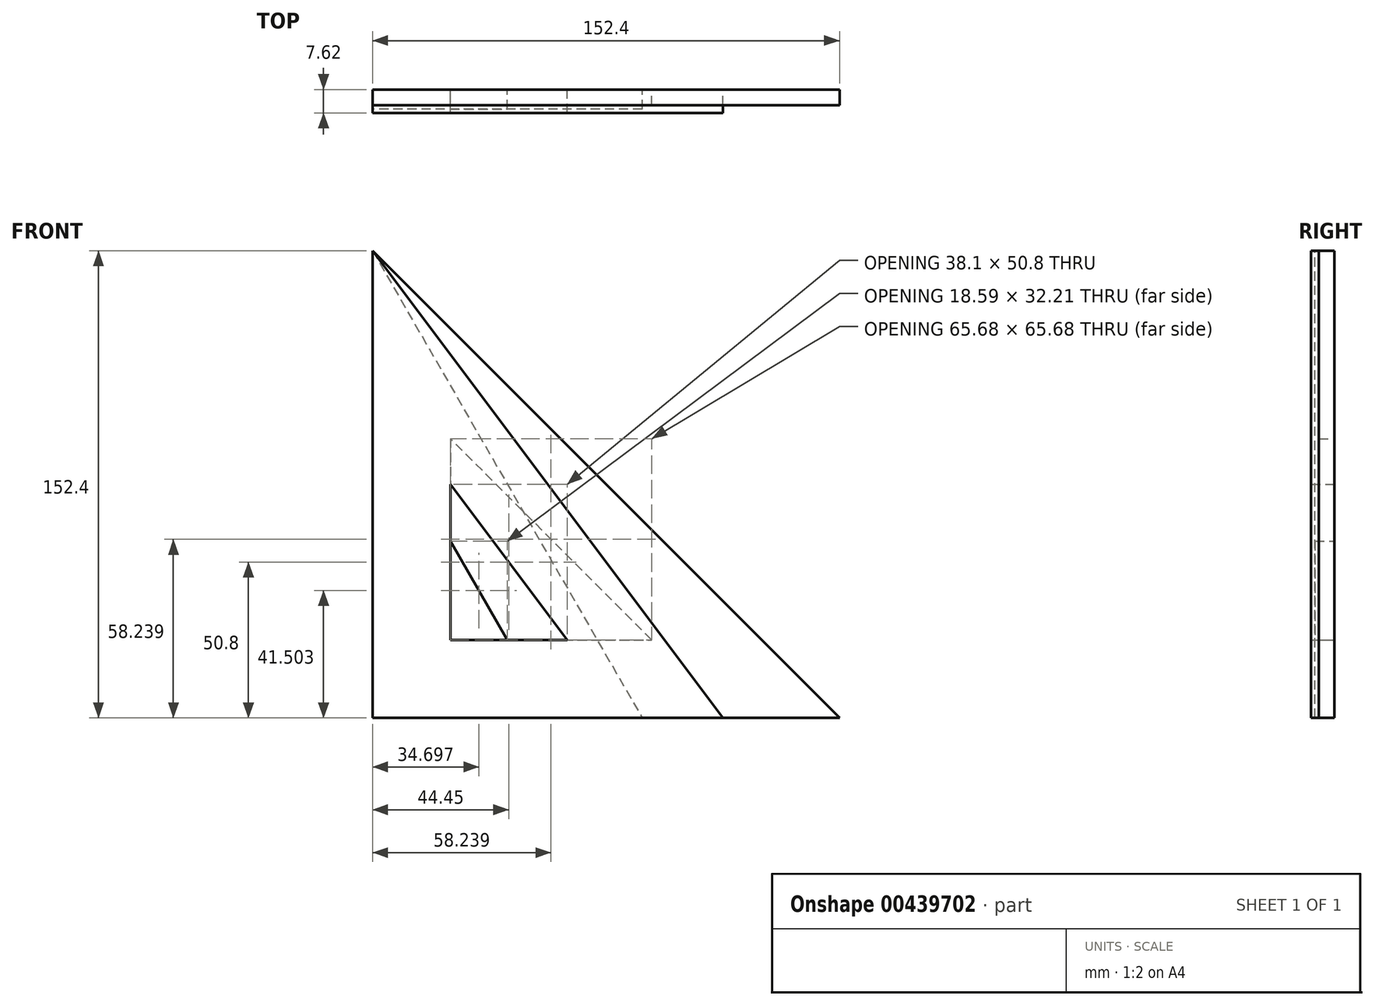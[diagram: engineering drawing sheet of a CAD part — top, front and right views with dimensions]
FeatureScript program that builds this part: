
annotation { "Feature Type Name" : "Feature", "Feature Type Description" : "" }
export const myFeature = defineFeature(function(context is Context, id is Id, definition is map)
    precondition{}
    {
        {
            var Q0;
            Q0=qCreatedBy(makeId("Front.planeOp"),FACE);
            var sketch = newSketch(context, id + "F0", { "sketchPlane" : qUnion([Q0])});
            skLineSegment(sketch, "E0", {"start": v(0, 0) * mm, "end": v(152.4, 0) * mm});
            skLineSegment(sketch, "E1", {"start": v(0, 152.4) * mm, "end": v(0, 0) * mm});
            skLineSegment(sketch, "E2", {"start": v(25.4, 25.4) * mm, "end": v(91.08, 25.4) * mm});
            skLineSegment(sketch, "E3", {"start": v(91.08, 25.4) * mm, "end": v(25.4, 91.08) * mm});
            skLineSegment(sketch, "E4", {"start": v(25.4, 91.08) * mm, "end": v(25.4, 25.4) * mm});
            skLineSegment(sketch, "E5", {"start": v(0, 152.4) * mm, "end": v(152.4, 0) * mm});
            skSolve(sketch);
        }
        {
            var Q0;
            Q0=makeQuery(id+"F0.imprint","IMPRINT",FACE,{"disambiguationData":[TD([[makeQuery(id+"F0.imprint","IMPRINT",EDGE,{"derivedFrom":sQuery(id+"F0.wireOp",EDGE,"E0")}),1.0]])]});
            extrude(context, id + "F1", {"entities" : qUnion([Q0]), "depth" : 5.08 * mm});
        }
        {
            var Q0;
            Q0=qCreatedBy(makeId("Front.planeOp"),FACE);
            var sketch = newSketch(context, id + "F2", { "sketchPlane" : qUnion([Q0])});
            skLineSegment(sketch, "E6", {"start": v(0, 0) * mm, "end": v(0, 152.4) * mm});
            skLineSegment(sketch, "E7", {"start": v(0, 152.4) * mm, "end": v(87.99, 0) * mm});
            skLineSegment(sketch, "E8", {"start": v(87.99, 0) * mm, "end": v(0, 0) * mm});
            skLineSegment(sketch, "E9", {"start": v(25.4, 25.4) * mm, "end": v(44, 25.4) * mm});
            skLineSegment(sketch, "E10", {"start": v(44, 25.4) * mm, "end": v(25.4, 57.6) * mm});
            skLineSegment(sketch, "E11", {"start": v(25.4, 57.6) * mm, "end": v(25.4, 25.4) * mm});
            skSolve(sketch);
        }
        {
            var Q0;
            Q0 = qSketchRegion(id + "F2", true);
            extrude(context, id + "F3", {"entities" : qUnion([Q0]), "depth" : 6.35 * mm});
        }
        {
            var Q0;
            Q0=qCreatedBy(makeId("Front.planeOp"),FACE);
            var sketch = newSketch(context, id + "F4", { "sketchPlane" : qUnion([Q0])});
            skLineSegment(sketch, "E12", {"start": v(0, 0) * mm, "end": v(0, 152.4) * mm});
            skLineSegment(sketch, "E13", {"start": v(0, 152.4) * mm, "end": v(114.3, 0) * mm});
            skLineSegment(sketch, "E14", {"start": v(114.3, 0) * mm, "end": v(0, 0) * mm});
            skLineSegment(sketch, "E15", {"start": v(25.4, 25.4) * mm, "end": v(63.5, 25.4) * mm});
            skLineSegment(sketch, "E16", {"start": v(63.5, 25.4) * mm, "end": v(25.4, 76.2) * mm});
            skLineSegment(sketch, "E17", {"start": v(25.4, 76.2) * mm, "end": v(25.4, 25.4) * mm});
            skSolve(sketch);
        }
        {
            var Q0;
            Q0 = qSketchRegion(id + "F4", true);
            extrude(context, id + "F5", {"entities" : qUnion([Q0]), "depth" : 7.62 * mm});
        }
    });
